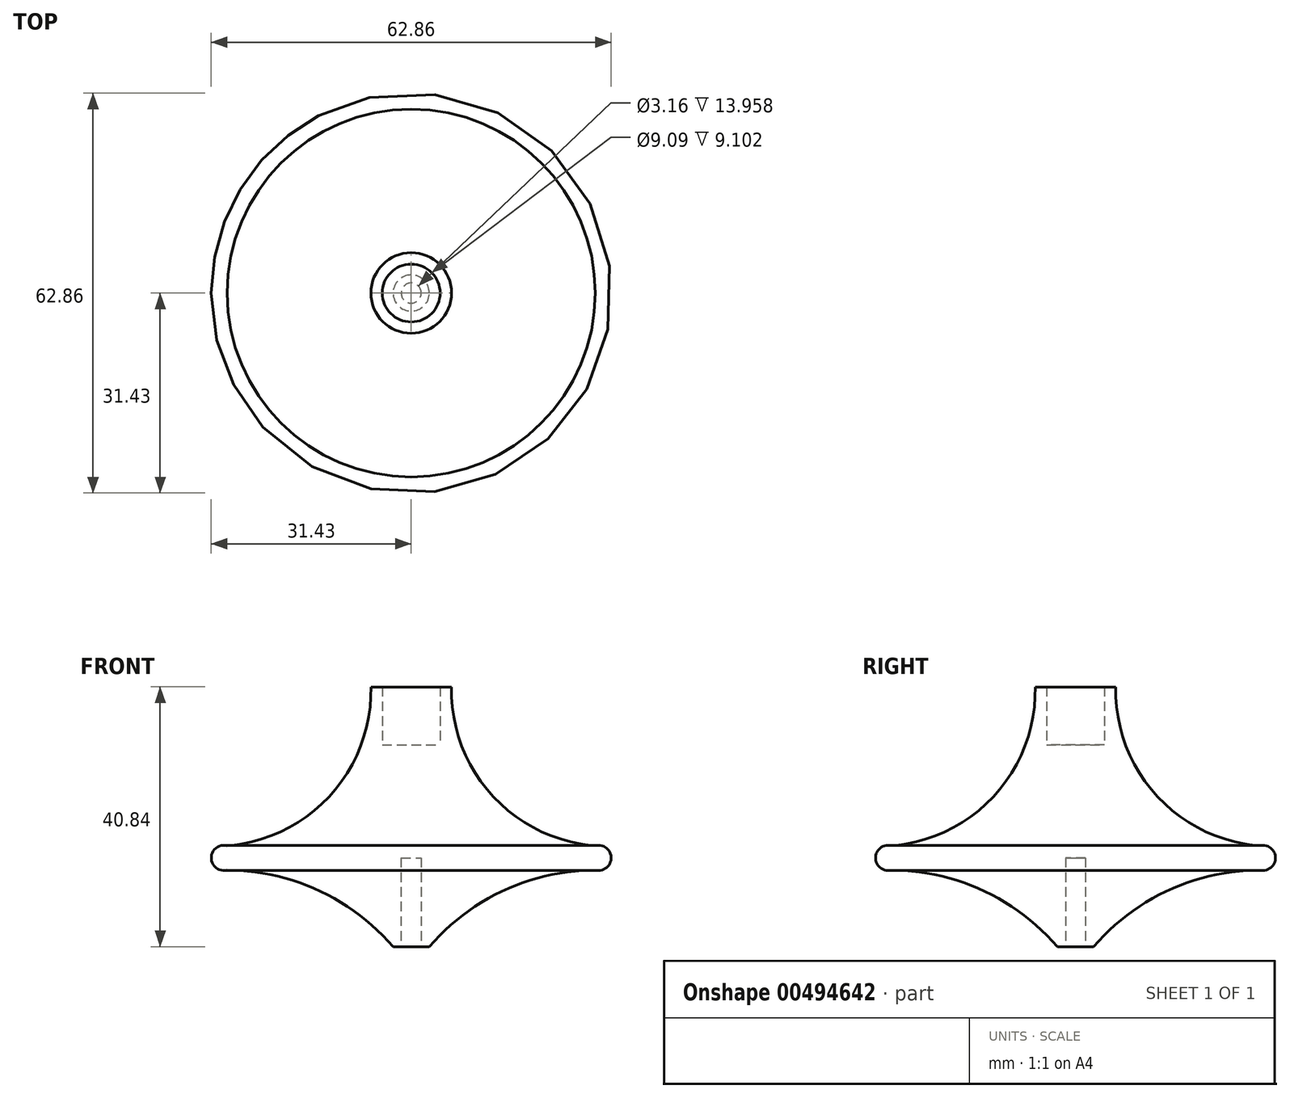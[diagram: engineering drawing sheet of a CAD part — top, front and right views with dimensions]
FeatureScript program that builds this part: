
annotation { "Feature Type Name" : "Feature", "Feature Type Description" : "" }
export const myFeature = defineFeature(function(context is Context, id is Id, definition is map)
    precondition{}
    {
        {
            var Q0;
            Q0=qCreatedBy(makeId("Front.planeOp"),FACE);
            var sketch = newSketch(context, id + "F0", { "sketchPlane" : qUnion([Q0])});
            skLineSegment(sketch, "E0", {"start": v(0, 0) * mm, "end": v(1.58, 0) * mm});
            skLineSegment(sketch, "E1", {"start": v(1.58, 0) * mm, "end": v(1.58, 13.96) * mm});
            skLineSegment(sketch, "E2", {"start": v(1.58, 13.96) * mm, "end": v(0, 13.96) * mm});
            skLineSegment(sketch, "E3", {"start": v(1.58, 0) * mm, "end": v(2.85, 0) * mm});
            skLineSegment(sketch, "E4", {"start": v(0, 13.96) * mm, "end": v(0, 31.73) * mm});
            skArc(sketch, "E5", {"start": v(28.92, 12.05) * mm, "mid": v(31.43, 13.95) * mm, "end": v(28.92, 15.86) * mm});
            skArc(sketch, "E6", {"start": v(28.92, 12.05) * mm, "mid": v(14.58, 8.84) * mm, "end": v(2.85, 0) * mm});
            skLineSegment(sketch, "E7", {"start": v(0, 31.73) * mm, "end": v(4.55, 31.73) * mm});
            skLineSegment(sketch, "E8", {"start": v(4.55, 31.73) * mm, "end": v(4.55, 40.84) * mm});
            skLineSegment(sketch, "E9", {"start": v(4.55, 40.84) * mm, "end": v(6.33, 40.84) * mm});
            skArc(sketch, "E10", {"start": v(6.33, 40.84) * mm, "mid": v(12.66, 23.85) * mm, "end": v(28.92, 15.86) * mm});
            skSolve(sketch);
        }
        {
            var Q0;
            {var subQ5=sQuery(id+"F0.wireOp",EDGE,"E4");Q0=makeQuery(id+"F0.imprint","IMPRINT",FACE,{"disambiguationData":[TD([[makeQuery(id+"F0.imprint","IMPRINT",EDGE,{"derivedFrom":subQ5}),-1.0]])]});}
            var Q1;
            {var subQ0=sQuery(id+"F0.wireOp",EDGE,"E5");var subQ1=sQuery(id+"F0.wireOp",EDGE,"CpjtOIoZ-9qsa-Smxm-wNF6-0vy4wL0vy6p2");var subQ2=makeQuery(id+"F0.imprint","INTERSECT",VERTEX,{"derivedFrom":[subQ1,subQ0]});Q1=makeQuery(id+"F0.imprint","IMPRINT",FACE,{"disambiguationData":[TD([[makeQuery(id+"F0.imprint","IMPRINT",EDGE,{"disambiguationData":[TD([[subQ2,1.0]])],"derivedFrom":subQ1}),-1.0]])]});}
            var Q2;
            {var subQ0=sQuery(id+"F0.wireOp",EDGE,"E5");var subQ1=sQuery(id+"F0.wireOp",EDGE,"CpjtOIoZ-9qsa-Smxm-wNF6-0vy4wL0vy6p2");var subQ2=makeQuery(id+"F0.imprint","INTERSECT",VERTEX,{"derivedFrom":[subQ1,subQ0]});Q2=makeQuery(id+"F0.imprint","IMPRINT",FACE,{"disambiguationData":[TD([[makeQuery(id+"F0.imprint","IMPRINT",EDGE,{"disambiguationData":[TD([[subQ2,1.0]])],"derivedFrom":subQ1}),1.0]])]});}
            var Q3;
            {var subQ4=sQuery(id+"F0.wireOp",EDGE,"E1");Q3=makeQuery(id+"F0.imprint","IMPRINT",FACE,{"disambiguationData":[TD([[makeQuery(id+"F0.imprint","IMPRINT",EDGE,{"derivedFrom":subQ4}),-1.0]])]});}
            var Q4;
            Q4=sQuery(id+"F0.wireOp",EDGE,"E4");
            revolve(context, id + "F1", {"entities" : qUnion([Q0, Q1, Q2, Q3]), "axis" : qUnion([Q4]), "revolveType" : RevolveType.FULL});
        }
    });
